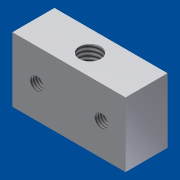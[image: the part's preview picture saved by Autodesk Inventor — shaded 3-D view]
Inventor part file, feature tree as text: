
AUTODESK INVENTOR PART (.ipt)
format: ipt  version: 2012 SP1 (Build 160190100, 190)  size: 102,400 bytes
history: native  units: in
note: dims shown in document units (in); Inventor stores cm internally (conversion verified against a paired STEP export)
features: sketch x3, hole x2, extrude x1
ambient origin geometry x8: Origin, YZ Plane, XZ Plane, XY Plane, X Axis, Y Axis, Z Axis, Center Point
bodies: Solid1 (feature_tree)
feature tree (6):
  extrude  "Extrusion1"  Depth=0.7874in
  hole  "Hole1"  [1 undecoded]
  hole  "Hole2"  [1 undecoded]
  sketch  "Sketch1"  dims[d0=1.378in d1=0.7874in]
  sketch  "Sketch2"  dims[d2=0.3937in d3=0.689in]
  sketch  "Sketch3"  dims[d4=0.5118in d5=0.0in d6=0.1654in d7=0.1654in d8=0.7874in d9=0.3937in d10=0.3937in d11=0.2953in d12=0.1628in d13=0.2362in d14=0.1575in d15=0.0787in d16=90.0deg d17=0.315in d18=0.8108in d19=0.2657in d20=0.689in d21=0.2559in d22=0.2617in d23=0.2362in d24=0.1575in d25=0.0787in d26=90.0deg d27=0.315in d28=0.8108in]
note: 2 required parameter values undecoded (feature->parameter linkage not recoverable at this tier; creation-order binding heuristic only, values carry confidence <= 0.55)
